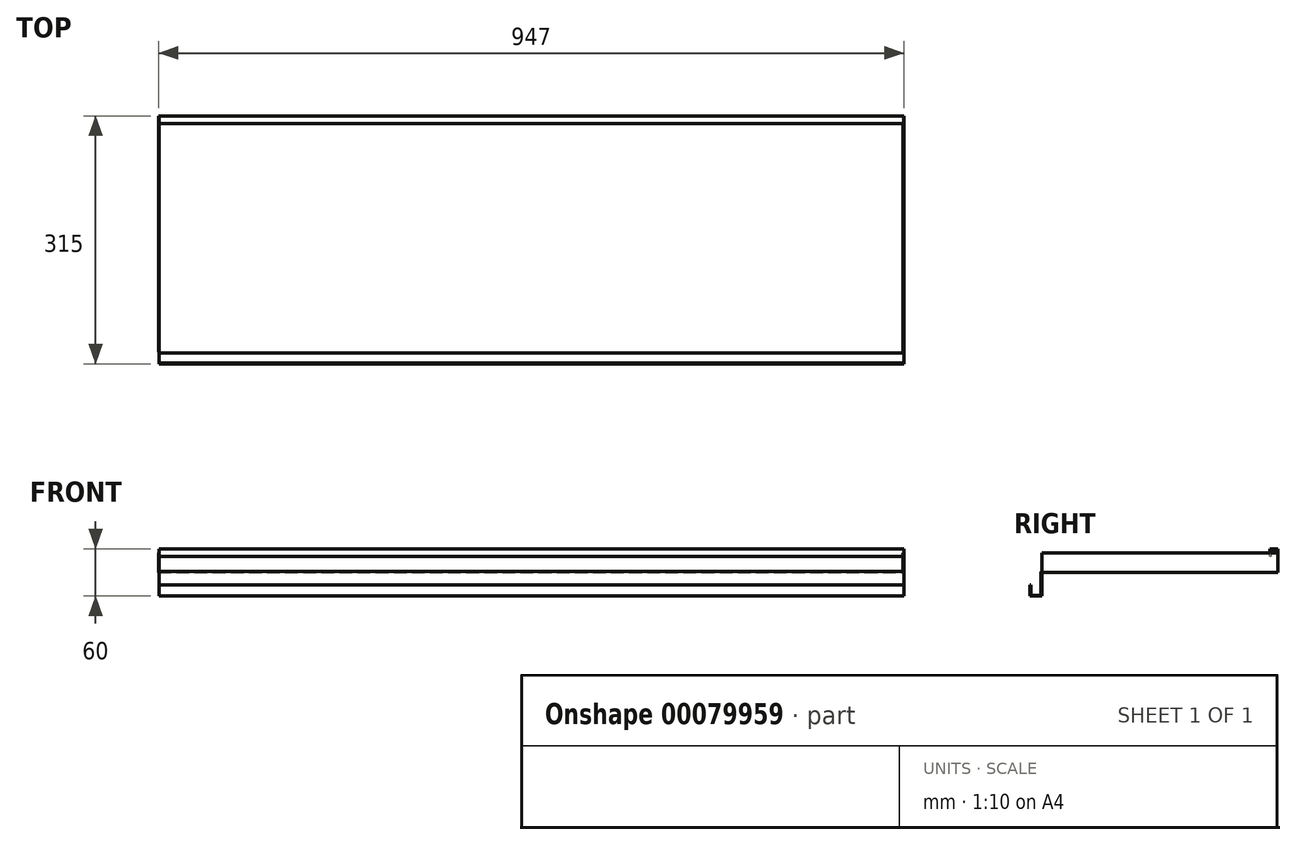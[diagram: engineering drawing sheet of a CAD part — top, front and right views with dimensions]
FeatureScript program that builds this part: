
annotation { "Feature Type Name" : "Feature", "Feature Type Description" : "" }
export const myFeature = defineFeature(function(context is Context, id is Id, definition is map)
    precondition{}
    {
        {
            var Q0;
            Q0=qCreatedBy(makeId("Front.planeOp"),FACE);
            var sketch = newSketch(context, id + "F0", { "sketchPlane" : qUnion([Q0])});
            skLineSegment(sketch, "E0", {"start": v(-474, 0) * mm, "end": v(473, 0) * mm});
            skLineSegment(sketch, "E1", {"start": v(473, 0) * mm, "end": v(473, 25) * mm});
            skLineSegment(sketch, "E2", {"start": v(473, 25) * mm, "end": v(472, 25) * mm});
            skLineSegment(sketch, "E3", {"start": v(472, 25) * mm, "end": v(472, 1) * mm});
            skLineSegment(sketch, "E4", {"start": v(472, 1) * mm, "end": v(-473, 1) * mm});
            skLineSegment(sketch, "E5", {"start": v(-473, 1) * mm, "end": v(-473, 25) * mm});
            skLineSegment(sketch, "E6", {"start": v(-473, 25) * mm, "end": v(-474, 25) * mm});
            skLineSegment(sketch, "E7", {"start": v(-474, 25) * mm, "end": v(-474, 0) * mm});
            skSolve(sketch);
        }
        {
            var Q0;
            Q0 = qSketchRegion(id + "F0", true);
            extrude(context, id + "F1", {"entities" : qUnion([Q0]), "depth" : 300 * mm});
        }
        {
            var Q0;
            Q0=qCreatedBy(makeId("Right.planeOp"),FACE);
            var sketch = newSketch(context, id + "F2", { "sketchPlane" : qUnion([Q0])});
            skLineSegment(sketch, "E8", {"start": v(-300, 0) * mm, "end": v(-300, -30) * mm});
            skLineSegment(sketch, "E9", {"start": v(-300, -30) * mm, "end": v(-315, -30) * mm});
            skLineSegment(sketch, "E10", {"start": v(-315, -30) * mm, "end": v(-315, -16) * mm});
            skLineSegment(sketch, "E11", {"start": v(-315, -16) * mm, "end": v(-314, -16) * mm});
            skLineSegment(sketch, "E12", {"start": v(-314, -16) * mm, "end": v(-314, -29) * mm});
            skLineSegment(sketch, "E13", {"start": v(-314, -29) * mm, "end": v(-301, -29) * mm});
            skLineSegment(sketch, "E14", {"start": v(-301, -29) * mm, "end": v(-301, 0) * mm});
            skLineSegment(sketch, "E15", {"start": v(-300, 0) * mm, "end": v(-300, 1) * mm});
            skArc(sketch, "E16", {"start": v(-300, 1) * mm, "mid": v(-300.7, 0.7) * mm, "end": v(-301, 0) * mm});
            skSolve(sketch);
        }
        {
            var Q0;
            Q0 = qSketchRegion(id + "F2", true);
            extrude(context, id + "F3", {"entities" : qUnion([Q0]), "operationType" : NewBodyOperationType.ADD, "depth" : 473 * mm, "hasSecondDirection" : true, "secondDirectionOppositeDirection" : true, "secondDirectionDepth" : 473 * mm});
        }
        {
            var Q0;
            Q0=qCreatedBy(makeId("Right.planeOp"),FACE);
            var sketch = newSketch(context, id + "F4", { "sketchPlane" : qUnion([Q0])});
            skLineSegment(sketch, "E17", {"start": v(0, 0) * mm, "end": v(0, 30) * mm});
            skLineSegment(sketch, "E18", {"start": v(0, 30) * mm, "end": v(-10, 30) * mm});
            skLineSegment(sketch, "E19", {"start": v(-10, 30) * mm, "end": v(-10, 20) * mm});
            skLineSegment(sketch, "E20", {"start": v(-10, 20) * mm, "end": v(-9, 20) * mm});
            skLineSegment(sketch, "E21", {"start": v(-9, 20) * mm, "end": v(-9, 29) * mm});
            skLineSegment(sketch, "E22", {"start": v(-9, 29) * mm, "end": v(-1, 29) * mm});
            skLineSegment(sketch, "E23", {"start": v(-1, 29) * mm, "end": v(-1, 0) * mm});
            skLineSegment(sketch, "E24", {"start": v(-1, 0) * mm, "end": v(0, 0) * mm});
            skSolve(sketch);
        }
        {
            var Q0;
            Q0 = qSketchRegion(id + "F4", true);
            extrude(context, id + "F5", {"entities" : qUnion([Q0]), "operationType" : NewBodyOperationType.ADD, "depth" : 473 * mm, "hasSecondDirection" : true, "secondDirectionOppositeDirection" : true, "secondDirectionDepth" : 473 * mm});
        }
    });
